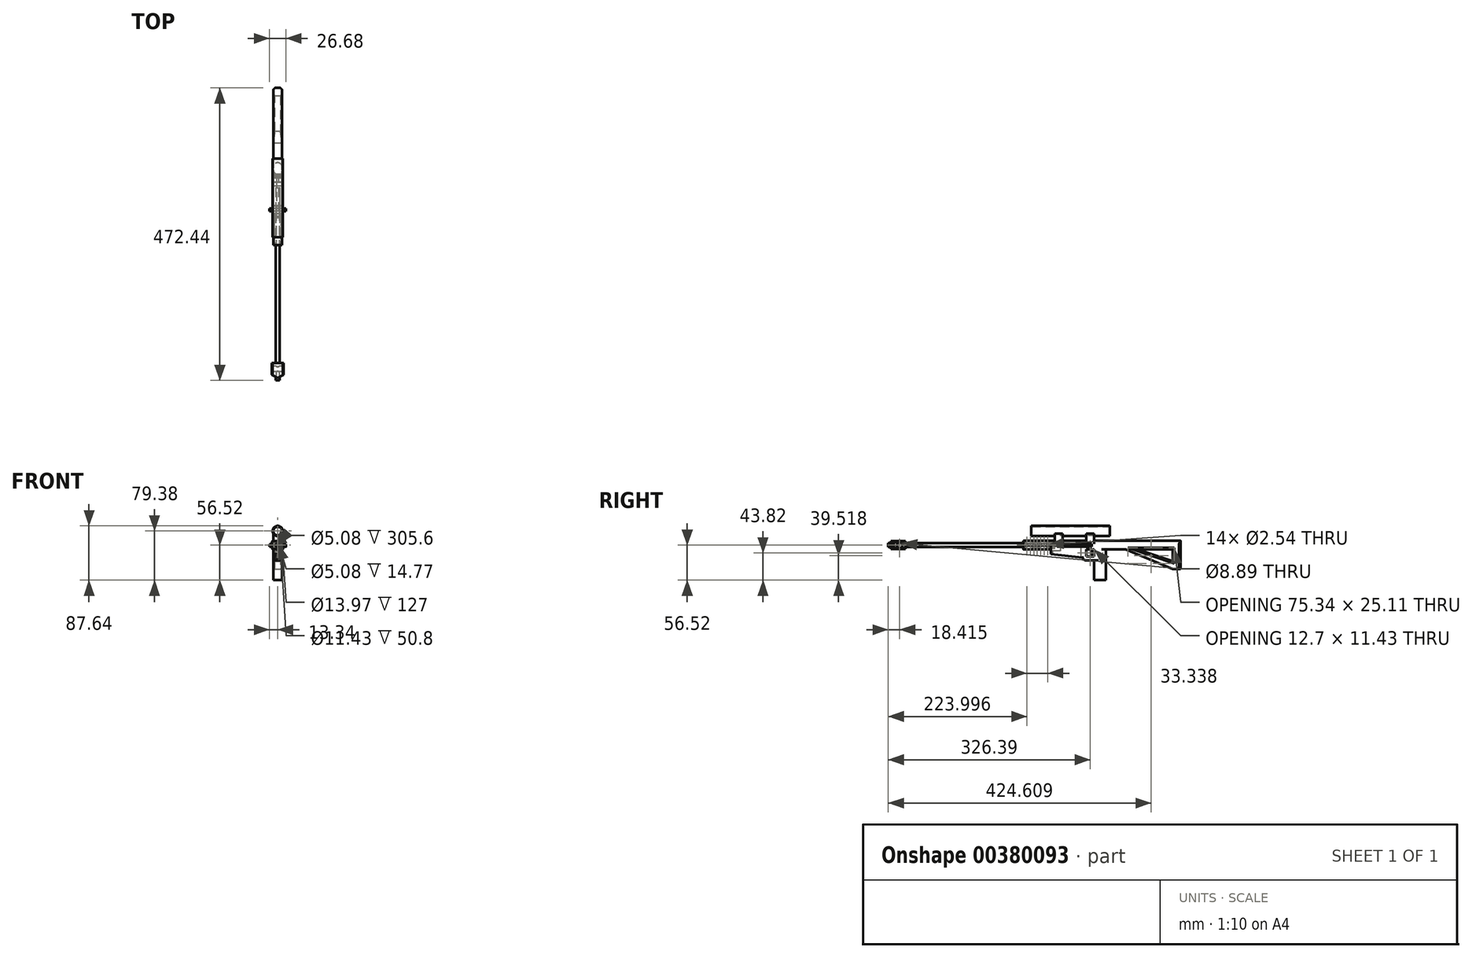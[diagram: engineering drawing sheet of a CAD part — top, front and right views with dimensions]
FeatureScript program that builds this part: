
annotation { "Feature Type Name" : "Feature", "Feature Type Description" : "" }
export const myFeature = defineFeature(function(context is Context, id is Id, definition is map)
    precondition{}
    {
        {
            var Q0;
            Q0=qCreatedBy(makeId("Front.planeOp"),FACE);
            var sketch = newSketch(context, id + "F0", { "sketchPlane" : qUnion([Q0])});
            skLineSegment(sketch, "E0.bottom", {"start": v(9.53, -6.35) * mm, "end": v(-9.53, -6.35) * mm});
            skLineSegment(sketch, "E0.top", {"start": v(9.53, 6.35) * mm, "end": v(-9.53, 6.35) * mm});
            skLineSegment(sketch, "E0.left", {"start": v(9.53, -6.35) * mm, "end": v(9.53, 6.35) * mm});
            skLineSegment(sketch, "E0.right", {"start": v(-9.53, -6.35) * mm, "end": v(-9.53, 6.35) * mm});
            skPoint(sketch, "E0.middle", {"position": v(0, 0) * mm});
            skSolve(sketch);
        }
        {
            var Q0;
            Q0 = qSketchRegion(id + "F0", true);
            extrude(context, id + "F1", {"entities" : qUnion([Q0]), "depth" : 25.4 * mm});
        }
        {
            var Q0;
            Q0=makeQuery(id+"F1.opExtrude","CAP_FACE",FACE,{"disambiguationData":[OSD([sQuery(id+"F0.wireOp",EDGE,"E0.bottom"),sQuery(id+"F0.wireOp",EDGE,"E0.top"),sQuery(id+"F0.wireOp",EDGE,"E0.left"),sQuery(id+"F0.wireOp",EDGE,"E0.right")])],"isStart":true});
            var sketch = newSketch(context, id + "F2", { "sketchPlane" : qUnion([Q0])});
            skCircle(sketch, "E1", {"center": v(0, 0) * mm, "radius": 3.18 * mm});
            skSolve(sketch);
        }
        {
            var Q0;
            Q0 = qSketchRegion(id + "F2", true);
            extrude(context, id + "F3", {"entities" : qUnion([Q0]), "operationType" : NewBodyOperationType.ADD, "depth" : 190.5 * mm});
        }
        {
            var Q0;
            Q0=makeQuery(id+"F3.opExtrude","CAP_FACE",FACE,{"disambiguationData":[OSD([sQuery(id+"F2.wireOp",EDGE,"E1")])],"isStart":false});
            var sketch = newSketch(context, id + "F4", { "sketchPlane" : qUnion([Q0])});
            skLineSegment(sketch, "E2.bottom", {"start": v(6.99, -6.99) * mm, "end": v(-6.99, -6.99) * mm});
            skLineSegment(sketch, "E2.top", {"start": v(6.98, 6.99) * mm, "end": v(-6.98, 6.99) * mm});
            skLineSegment(sketch, "E2.left", {"start": v(6.99, -6.99) * mm, "end": v(6.99, 6.98) * mm});
            skLineSegment(sketch, "E2.right", {"start": v(-6.99, -6.99) * mm, "end": v(-6.99, 6.98) * mm});
            skPoint(sketch, "E2.middle", {"position": v(0, 0) * mm});
            skSolve(sketch);
        }
        {
            var Q0;
            Q0 = qSketchRegion(id + "F4", true);
            extrude(context, id + "F5", {"entities" : qUnion([Q0]), "operationType" : NewBodyOperationType.ADD, "depth" : 254 * mm});
        }
        {
            var Q0;
            Q0=makeQuery(id+"F5.opExtrude","SWEPT_FACE",FACE,{"disambiguationData":[OSD([sQuery(id+"F4.wireOp",EDGE,"E2.right")])]});
            var sketch = newSketch(context, id + "F6", { "sketchPlane" : qUnion([Q0])});
            skLineSegment(sketch, "E3", {"start": v(444.5, -6.99) * mm, "end": v(444.5, -38.74) * mm});
            skLineSegment(sketch, "E4", {"start": v(444.5, -38.74) * mm, "end": v(431.8, -38.74) * mm});
            skLineSegment(sketch, "E5", {"start": v(431.8, -38.74) * mm, "end": v(431.8, -6.99) * mm});
            skSolve(sketch);
        }
        {
            var Q0;
            Q0 = qSketchRegion(id + "F6", true);
            var Q1;
            {var subQ0=sQuery(id+"F6.wireOp",EDGE,"E3");Q1=makeQuery(id+"F6.imprint","IMPRINT",FACE,{"disambiguationData":[TD([[makeQuery(id+"F6.imprint","IMPRINT",EDGE,{"derivedFrom":subQ0}),-1.0]])]});}
            extrude(context, id + "F7", {"entities" : qUnion([Q0, Q1]), "operationType" : NewBodyOperationType.ADD, "depth" : -13.97 * mm});
        }
        {
            var Q0;
            {var subQ0=sQuery(id+"F4.wireOp",EDGE,"E2.right");Q0=makeQuery(id+"F7.boolean.opBoolean","MERGE",FACE,{"derivedFrom":[makeQuery(id+"F5.opExtrude","SWEPT_FACE",FACE,{"disambiguationData":[OSD([subQ0])]}),makeQuery(id+"F7.opExtrude","CAP_FACE",FACE,{"disambiguationData":[OSD([sQuery(id+"F4.wireOp",EDGE,"E2.bottom"),subQ0,sQuery(id+"F6.wireOp",EDGE,"E3"),sQuery(id+"F6.wireOp",EDGE,"E4"),sQuery(id+"F6.wireOp",EDGE,"E5")])],"isStart":true})]});}
            var sketch = newSketch(context, id + "F8", { "sketchPlane" : qUnion([Q0])});
            skLineSegment(sketch, "E6", {"start": v(431.8, -38.74) * mm, "end": v(355.6, -6.98) * mm});
            skLineSegment(sketch, "E7", {"start": v(431.8, -38.74) * mm, "end": v(431.8, -26.04) * mm});
            skLineSegment(sketch, "E8", {"start": v(431.8, -26.03) * mm, "end": v(374.65, -6.98) * mm});
            skLineSegment(sketch, "E9", {"start": v(374.65, -6.99) * mm, "end": v(355.6, -6.99) * mm});
            skSolve(sketch);
        }
        {
            var Q0;
            Q0 = qSketchRegion(id + "F8", true);
            extrude(context, id + "F9", {"entities" : qUnion([Q0]), "operationType" : NewBodyOperationType.ADD, "depth" : -13.97 * mm});
        }
        {
            var Q0;
            Q0=makeQuery(id+"F9.boolean.opBoolean","MERGE",FACE,{"derivedFrom":[makeQuery(id+"F7.boolean.opBoolean","MERGE",FACE,{"derivedFrom":[makeQuery(id+"F5.opExtrude","SWEPT_FACE",FACE,{"disambiguationData":[OSD([sQuery(id+"F4.wireOp",EDGE,"E2.left")])]}),makeQuery(id+"F7.opExtrude","CAP_FACE",FACE,{"disambiguationData":[OSD([sQuery(id+"F4.wireOp",EDGE,"E2.bottom"),sQuery(id+"F4.wireOp",EDGE,"E2.right"),sQuery(id+"F6.wireOp",EDGE,"E3"),sQuery(id+"F6.wireOp",EDGE,"E4"),sQuery(id+"F6.wireOp",EDGE,"E5")])],"isStart":false})]}),makeQuery(id+"F9.opExtrude","CAP_FACE",FACE,{"disambiguationData":[OSD([sQuery(id+"F8.wireOp",EDGE,"E6"),sQuery(id+"F8.wireOp",EDGE,"E7"),sQuery(id+"F8.wireOp",EDGE,"E8"),sQuery(id+"F8.wireOp",EDGE,"E9")])],"isStart":false})]});
            var sketch = newSketch(context, id + "F10", { "sketchPlane" : qUnion([Q0])});
            skLineSegment(sketch, "E10", {"start": v(-444.5, 6.98) * mm, "end": v(-190.5, 6.98) * mm});
            skLineSegment(sketch, "E11", {"start": v(-190.5, 6.98) * mm, "end": v(-317.5, 6.98) * mm});
            skLineSegment(sketch, "E12", {"start": v(-317.5, 6.98) * mm, "end": v(-317.5, -43.82) * mm});
            skLineSegment(sketch, "E13", {"start": v(-317.5, -43.82) * mm, "end": v(-304.8, -43.82) * mm});
            skLineSegment(sketch, "E14", {"start": v(-304.8, -43.82) * mm, "end": v(-304.8, 6.98) * mm});
            skLineSegment(sketch, "E15", {"start": v(-304.8, -18.42) * mm, "end": v(-292.1, -18.42) * mm});
            skLineSegment(sketch, "E16", {"start": v(-292.1, -18.42) * mm, "end": v(-292.1, -6.99) * mm});
            skLineSegment(sketch, "E17", {"start": v(-292.1, -6.99) * mm, "end": v(-285.75, -6.99) * mm});
            skLineSegment(sketch, "E18", {"start": v(-285.75, -6.99) * mm, "end": v(-285.75, -24.77) * mm});
            skLineSegment(sketch, "E19", {"start": v(-285.75, -24.77) * mm, "end": v(-304.8, -24.77) * mm});
            skLineSegment(sketch, "E20", {"start": v(-285.75, -6.99) * mm, "end": v(-280.67, -6.99) * mm});
            skLineSegment(sketch, "E21", {"start": v(-304.8, -43.82) * mm, "end": v(-304.8, -56.52) * mm});
            skLineSegment(sketch, "E22", {"start": v(-317.5, -43.82) * mm, "end": v(-317.5, -56.52) * mm});
            skLineSegment(sketch, "E23", {"start": v(-304.8, -56.52) * mm, "end": v(-317.5, -56.52) * mm});
            skLineSegment(sketch, "E24", {"start": v(-317.5, -56.52) * mm, "end": v(-323.85, -56.52) * mm});
            skLineSegment(sketch, "E25", {"start": v(-323.85, -56.52) * mm, "end": v(-323.85, -6.99) * mm});
            skSolve(sketch);
        }
        {
            var Q0;
            Q0 = qSketchRegion(id + "F10", true);
            var Q1;
            {var subQ8=sQuery(id+"F10.wireOp",EDGE,"E22");Q1=makeQuery(id+"F10.imprint","IMPRINT",FACE,{"disambiguationData":[TD([[makeQuery(id+"F10.imprint","IMPRINT",EDGE,{"derivedFrom":subQ8}),-1.0]])]});}
            extrude(context, id + "F11", {"entities" : qUnion([Q0, Q1]), "operationType" : NewBodyOperationType.ADD, "depth" : -13.97 * mm});
        }
        {
            var Q0;
            Q0=makeQuery(id+"F11.opExtrude","SWEPT_EDGE",EDGE,{"disambiguationData":[OSD([sQuery(id+"F10.wireOp",EDGE,"E18"),sQuery(id+"F10.wireOp",EDGE,"E19")])]});
            fillet(context, id + "F12", {"entities" : qUnion([Q0]), "radius" : 6.35 * mm, "tangentPropagation" : true, "allowEdgeOverflow" : false});
        }
        {
            var Q0;
            Q0=makeQuery(id+"F11.boolean.opBoolean","MERGE",FACE,{"derivedFrom":[makeQuery(id+"F9.boolean.opBoolean","MERGE",FACE,{"derivedFrom":[makeQuery(id+"F7.boolean.opBoolean","MERGE",FACE,{"derivedFrom":[makeQuery(id+"F5.opExtrude","SWEPT_FACE",FACE,{"disambiguationData":[OSD([sQuery(id+"F4.wireOp",EDGE,"E2.left")])]}),makeQuery(id+"F7.opExtrude","CAP_FACE",FACE,{"disambiguationData":[OSD([sQuery(id+"F4.wireOp",EDGE,"E2.bottom"),sQuery(id+"F4.wireOp",EDGE,"E2.right"),sQuery(id+"F6.wireOp",EDGE,"E3"),sQuery(id+"F6.wireOp",EDGE,"E4"),sQuery(id+"F6.wireOp",EDGE,"E5")])],"isStart":false})]}),makeQuery(id+"F9.opExtrude","CAP_FACE",FACE,{"disambiguationData":[OSD([sQuery(id+"F8.wireOp",EDGE,"E6"),sQuery(id+"F8.wireOp",EDGE,"E7"),sQuery(id+"F8.wireOp",EDGE,"E8"),sQuery(id+"F8.wireOp",EDGE,"E9")])],"isStart":false})]}),makeQuery(id+"F11.opExtrude","CAP_FACE",FACE,{"disambiguationData":[OSD([sQuery(id+"F10.wireOp",EDGE,"E11"),sQuery(id+"F10.wireOp",EDGE,"E12"),sQuery(id+"F10.wireOp",EDGE,"E13"),sQuery(id+"F10.wireOp",EDGE,"E14"),sQuery(id+"F10.wireOp",EDGE,"E15"),sQuery(id+"F10.wireOp",EDGE,"E16"),sQuery(id+"F10.wireOp",EDGE,"E17"),sQuery(id+"F10.wireOp",EDGE,"E18"),sQuery(id+"F10.wireOp",EDGE,"E19")])],"isStart":true})]});
            var sketch = newSketch(context, id + "F13", { "sketchPlane" : qUnion([Q0])});
            skLineSegment(sketch, "E26", {"start": v(-234.95, -22.23) * mm, "end": v(-234.95, -6.99) * mm});
            skLineSegment(sketch, "E27", {"start": v(-234.95, -22.23) * mm, "end": v(-285.75, -22.23) * mm});
            skLineSegment(sketch, "E28", {"start": v(-285.75, -22.23) * mm, "end": v(-285.75, -6.99) * mm});
            skSolve(sketch);
        }
        {
            var Q0;
            Q0 = qSketchRegion(id + "F13", true);
            var Q1;
            {var subQ0=sQuery(id+"F13.wireOp",EDGE,"gqdgmxWL-FIIV-5ZZU-RBbH-KmW0Z6Do0HDY");Q1=makeQuery(id+"F13.imprint","IMPRINT",FACE,{"disambiguationData":[TD([[makeQuery(id+"F13.imprint","IMPRINT",EDGE,{"derivedFrom":subQ0}),1.0]])]});}
            var Q2;
            {var subQ17=sQuery(id+"F13.wireOp",EDGE,"E26");Q2=makeQuery(id+"F13.imprint","IMPRINT",FACE,{"disambiguationData":[TD([[makeQuery(id+"F13.imprint","IMPRINT",EDGE,{"derivedFrom":subQ17}),1.0]])]});}
            extrude(context, id + "F14", {"entities" : qUnion([Q0, Q1, Q2]), "operationType" : NewBodyOperationType.ADD, "depth" : -13.97 * mm});
        }
        {
            var Q0;
            {var subQ0=sQuery(id+"F4.wireOp",EDGE,"E2.left");var subQ1=sQuery(id+"F4.wireOp",EDGE,"E2.bottom");Q0=makeQuery(id+"F14.boolean.opBoolean","MERGE",FACE,{"derivedFrom":[makeQuery(id+"F11.boolean.opBoolean","MERGE",FACE,{"derivedFrom":[makeQuery(id+"F9.boolean.opBoolean","MERGE",FACE,{"derivedFrom":[makeQuery(id+"F7.boolean.opBoolean","MERGE",FACE,{"derivedFrom":[makeQuery(id+"F5.opExtrude","SWEPT_FACE",FACE,{"disambiguationData":[OSD([subQ0])]}),makeQuery(id+"F7.opExtrude","CAP_FACE",FACE,{"disambiguationData":[OSD([subQ1,sQuery(id+"F4.wireOp",EDGE,"E2.right"),sQuery(id+"F6.wireOp",EDGE,"E3"),sQuery(id+"F6.wireOp",EDGE,"E4"),sQuery(id+"F6.wireOp",EDGE,"E5")])],"isStart":false})]}),makeQuery(id+"F9.opExtrude","CAP_FACE",FACE,{"disambiguationData":[OSD([sQuery(id+"F8.wireOp",EDGE,"E6"),sQuery(id+"F8.wireOp",EDGE,"E7"),sQuery(id+"F8.wireOp",EDGE,"E8"),sQuery(id+"F8.wireOp",EDGE,"E9")])],"isStart":false})]}),makeQuery(id+"F11.opExtrude","CAP_FACE",FACE,{"disambiguationData":[OSD([sQuery(id+"F10.wireOp",EDGE,"E11"),sQuery(id+"F10.wireOp",EDGE,"E12"),sQuery(id+"F10.wireOp",EDGE,"E13"),sQuery(id+"F10.wireOp",EDGE,"E14"),sQuery(id+"F10.wireOp",EDGE,"E15"),sQuery(id+"F10.wireOp",EDGE,"E16"),sQuery(id+"F10.wireOp",EDGE,"E17"),sQuery(id+"F10.wireOp",EDGE,"E18"),sQuery(id+"F10.wireOp",EDGE,"E19")])],"isStart":true})]}),makeQuery(id+"F14.opExtrude","CAP_FACE",FACE,{"disambiguationData":[OSD([subQ1,subQ0,sQuery(id+"F13.wireOp",EDGE,"gqdgmxWL-FIIV-5ZZU-RBbH-KmW0Z6Do0HDY"),sQuery(id+"F13.wireOp",EDGE,"u0oC4iEc-4FHG-jWvm-i2Hm-SS8I0tg0rfsX"),sQuery(id+"F13.wireOp",EDGE,"E26")])],"isStart":true})]});}
            var sketch = newSketch(context, id + "F15", { "sketchPlane" : qUnion([Q0])});
            skLineSegment(sketch, "E29", {"start": v(-304.8, -6.99) * mm, "end": v(-304.8, 18.41) * mm});
            skLineSegment(sketch, "E30", {"start": v(-292.1, -6.99) * mm, "end": v(-292.1, 18.41) * mm});
            skLineSegment(sketch, "E31", {"start": v(-304.8, 18.41) * mm, "end": v(-292.1, 18.41) * mm});
            skLineSegment(sketch, "E32", {"start": v(-292.1, -6.99) * mm, "end": v(-254, -6.99) * mm});
            skLineSegment(sketch, "E33", {"start": v(-254, -6.99) * mm, "end": v(-254, 18.41) * mm});
            skLineSegment(sketch, "E34", {"start": v(-254, 18.41) * mm, "end": v(-241.3, 18.41) * mm});
            skLineSegment(sketch, "E35", {"start": v(-241.3, 18.41) * mm, "end": v(-241.3, 6.98) * mm});
            skSolve(sketch);
        }
        {
            var Q0;
            Q0 = qSketchRegion(id + "F15", true);
            var Q1;
            {var subQ0=sQuery(id+"F15.wireOp",EDGE,"E31");Q1=makeQuery(id+"F15.imprint","IMPRINT",FACE,{"disambiguationData":[TD([[makeQuery(id+"F15.imprint","IMPRINT",EDGE,{"derivedFrom":subQ0}),-1.0]])]});}
            var Q2;
            {var subQ0=sQuery(id+"F15.wireOp",EDGE,"E34");Q2=makeQuery(id+"F15.imprint","IMPRINT",FACE,{"disambiguationData":[TD([[makeQuery(id+"F15.imprint","IMPRINT",EDGE,{"derivedFrom":subQ0}),-1.0]])]});}
            extrude(context, id + "F16", {"entities" : qUnion([Q0, Q1, Q2]), "operationType" : NewBodyOperationType.ADD, "depth" : -13.97 * mm});
        }
        {
            var Q0;
            Q0=makeQuery(id+"F16.opExtrude","SWEPT_FACE",FACE,{"disambiguationData":[OSD([sQuery(id+"F15.wireOp",EDGE,"E29")])]});
            var sketch = newSketch(context, id + "F17", { "sketchPlane" : qUnion([Q0])});
            skLineSegment(sketch, "E36", {"start": v(0, 0) * mm, "end": v(0, 22.86) * mm});
            skPoint(sketch, "E36.endSnap0", {"position": v(0, 18.41) * mm});
            skCircle(sketch, "E37", {"center": v(0, 22.86) * mm, "radius": 8.26 * mm});
            skSolve(sketch);
        }
        {
            var Q0;
            Q0 = qSketchRegion(id + "F17", true);
            extrude(context, id + "F18", {"entities" : qUnion([Q0]), "operationType" : NewBodyOperationType.ADD, "depth" : 25.4 * mm, "hasSecondDirection" : true, "secondDirectionOppositeDirection" : true, "secondDirectionDepth" : 101.6 * mm});
        }
        {
            var Q0;
            Q0=makeQuery(id+"F14.opExtrude","SWEPT_FACE",FACE,{"disambiguationData":[OSD([sQuery(id+"F13.wireOp",EDGE,"E27")])]});
            var sketch = newSketch(context, id + "F19", { "sketchPlane" : qUnion([Q0])});
            skLineSegment(sketch, "E38", {"start": v(-3.5, -283.21) * mm, "end": v(3.5, -283.21) * mm});
            skLineSegment(sketch, "E39", {"start": v(-3.5, -237.49) * mm, "end": v(3.5, -237.49) * mm});
            skLineSegment(sketch, "E40", {"start": v(-3.5, -283.21) * mm, "end": v(-3.5, -237.49) * mm});
            skLineSegment(sketch, "E41", {"start": v(3.5, -237.49) * mm, "end": v(3.5, -283.21) * mm});
            skLineSegment(sketch, "E42", {"start": v(3.5, -283.21) * mm, "end": v(3.5, -237.49) * mm});
            skLineSegment(sketch, "E43", {"start": v(3.5, -237.49) * mm, "end": v(-3.5, -237.49) * mm});
            skLineSegment(sketch, "E44", {"start": v(-3.5, -237.49) * mm, "end": v(-3.5, -283.21) * mm});
            skSolve(sketch);
        }
        {
            var Q0;
            Q0 = qSketchRegion(id + "F19", true);
            extrude(context, id + "F20", {"entities" : qUnion([Q0]), "operationType" : NewBodyOperationType.REMOVE, "oppositeDirection" : true, "depth" : 12.7 * mm});
        }
        {
            var Q0;
            Q0=makeQuery(id+"F14.opExtrude","SWEPT_EDGE",EDGE,{"disambiguationData":[OSD([sQuery(id+"F13.wireOp",EDGE,"E26"),sQuery(id+"F13.wireOp",EDGE,"E27")])]});
            chamfer(context, id + "F21", {"entities" : qUnion([Q0]), "chamferType" : ChamferType.OFFSET_ANGLE, "width" : 7.62 * mm, "oppositeDirection" : true, "angle" : 84 * degree, "tangentPropagation" : true});
        }
        {
            var Q0;
            Q0=makeQuery(id+"F7.boolean.opBoolean","MERGE",EDGE,{"derivedFrom":[makeQuery(id+"F5.opExtrude","CAP_EDGE",EDGE,{"disambiguationData":[OSD([sQuery(id+"F4.wireOp",EDGE,"E2.left")])],"isStart":false}),makeQuery(id+"F7.opExtrude","CAP_EDGE",EDGE,{"disambiguationData":[OSD([sQuery(id+"F6.wireOp",EDGE,"E3")])],"isStart":false})]});
            var Q1;
            Q1=makeQuery(id+"F7.boolean.opBoolean","MERGE",EDGE,{"derivedFrom":[makeQuery(id+"F5.opExtrude","CAP_EDGE",EDGE,{"disambiguationData":[OSD([sQuery(id+"F4.wireOp",EDGE,"E2.right")])],"isStart":false}),makeQuery(id+"F7.opExtrude","CAP_EDGE",EDGE,{"disambiguationData":[OSD([sQuery(id+"F6.wireOp",EDGE,"E3")])],"isStart":true})]});
            chamfer(context, id + "F22", {"entities" : qUnion([Q0, Q1]), "width" : 2.54 * mm, "tangentPropagation" : true});
        }
        {
            var Q0;
            {var subQ1=sQuery(id+"F4.wireOp",EDGE,"E2.left");var subQ2=sQuery(id+"F4.wireOp",EDGE,"E2.top");var subQ3=sQuery(id+"F6.wireOp",EDGE,"E3");Q0=makeQuery(id+"F16.boolean.opBoolean","SPLIT",EDGE,{"disambiguationData":[TD([makeQuery(id+"F7.opExtrude","SWEPT_FACE",FACE,{"disambiguationData":[OSD([subQ3])]})])],"derivedFrom":makeQuery(id+"F5.opExtrude","SWEPT_EDGE",EDGE,{"disambiguationData":[OSD([subQ2,subQ1])]})});}
            var Q1;
            {var subQ2=sQuery(id+"F4.wireOp",EDGE,"E2.top");var subQ3=sQuery(id+"F4.wireOp",EDGE,"E2.right");var subQ5=sQuery(id+"F6.wireOp",EDGE,"E3");Q1=makeQuery(id+"F16.boolean.opBoolean","SPLIT",EDGE,{"disambiguationData":[TD([makeQuery(id+"F7.opExtrude","SWEPT_FACE",FACE,{"disambiguationData":[OSD([subQ5])]})])],"derivedFrom":makeQuery(id+"F5.opExtrude","SWEPT_EDGE",EDGE,{"disambiguationData":[OSD([subQ2,subQ3])]})});}
            var Q2;
            {var subQ2=sQuery(id+"F4.wireOp",EDGE,"E2.left");var subQ3=sQuery(id+"F4.wireOp",EDGE,"E2.top");var subQ4=sQuery(id+"F15.wireOp",EDGE,"E30");Q2=makeQuery(id+"F16.boolean.opBoolean","SPLIT",EDGE,{"disambiguationData":[TD([makeQuery(id+"F16.opExtrude","SWEPT_FACE",FACE,{"disambiguationData":[OSD([subQ4])]})])],"derivedFrom":makeQuery(id+"F5.opExtrude","SWEPT_EDGE",EDGE,{"disambiguationData":[OSD([subQ3,subQ2])]})});}
            var Q3;
            {var subQ0=sQuery(id+"F4.wireOp",EDGE,"E2.right");var subQ2=sQuery(id+"F4.wireOp",EDGE,"E2.top");var subQ5=sQuery(id+"F15.wireOp",EDGE,"E30");Q3=makeQuery(id+"F16.boolean.opBoolean","SPLIT",EDGE,{"disambiguationData":[TD([makeQuery(id+"F16.opExtrude","SWEPT_FACE",FACE,{"disambiguationData":[OSD([subQ5])]})])],"derivedFrom":makeQuery(id+"F5.opExtrude","SWEPT_EDGE",EDGE,{"disambiguationData":[OSD([subQ2,subQ0])]})});}
            fillet(context, id + "F23", {"entities" : qUnion([Q0, Q1, Q2, Q3]), "radius" : 5.08 * mm, "tangentPropagation" : true, "allowEdgeOverflow" : false});
        }
        {
            var Q0;
            Q0=makeQuery(id+"F1.opExtrude","CAP_EDGE",EDGE,{"disambiguationData":[OSD([sQuery(id+"F0.wireOp",EDGE,"E0.left")])],"isStart":false});
            var Q1;
            Q1=makeQuery(id+"F1.opExtrude","CAP_EDGE",EDGE,{"disambiguationData":[OSD([sQuery(id+"F0.wireOp",EDGE,"E0.right")])],"isStart":false});
            chamfer(context, id + "F24", {"entities" : qUnion([Q0, Q1]), "chamferType" : ChamferType.OFFSET_ANGLE, "width" : 6.35 * mm, "oppositeDirection" : true, "angle" : 64 * degree, "tangentPropagation" : true});
        }
        {
            var Q0;
            Q0=qCreatedBy(makeId("Front.planeOp"),FACE);
            var sketch = newSketch(context, id + "F25", { "sketchPlane" : qUnion([Q0])});
            skCircle(sketch, "E45", {"center": v(0, 0) * mm, "radius": 3.18 * mm});
            skSolve(sketch);
        }
        {
            var Q0;
            Q0 = qSketchRegion(id + "F25", true);
            extrude(context, id + "F26", {"entities" : qUnion([Q0]), "operationType" : NewBodyOperationType.ADD, "depth" : 27.94 * mm});
        }
        {
            var Q0;
            Q0=makeQuery(id+"F1.opExtrude","SWEPT_FACE",FACE,{"disambiguationData":[OSD([sQuery(id+"F0.wireOp",EDGE,"E0.right")])]});
            var sketch = newSketch(context, id + "F27", { "sketchPlane" : qUnion([Q0])});
            skLineSegment(sketch, "E46", {"start": v(0, 0) * mm, "end": v(19.05, 0) * mm});
            skLineSegment(sketch, "E47", {"start": v(19.05, 0) * mm, "end": v(9.53, 0) * mm});
            skCircle(sketch, "E48", {"center": v(9.53, 0) * mm, "radius": 4.45 * mm});
            skSolve(sketch);
        }
        {
            var Q0;
            Q0 = qSketchRegion(id + "F27", true);
            extrude(context, id + "F28", {"entities" : qUnion([Q0]), "operationType" : NewBodyOperationType.REMOVE, "oppositeDirection" : true, "depth" : 50.8 * mm});
        }
        {
            var Q0;
            Q0=makeQuery(id+"F26.opExtrude","CAP_FACE",FACE,{"disambiguationData":[OSD([sQuery(id+"F25.wireOp",EDGE,"E45")])],"isStart":false});
            var sketch = newSketch(context, id + "F29", { "sketchPlane" : qUnion([Q0])});
            skCircle(sketch, "E49", {"center": v(0, 0) * mm, "radius": 2.54 * mm});
            skSolve(sketch);
        }
        {
            var Q0;
            Q0 = qSketchRegion(id + "F29", true);
            extrude(context, id + "F30", {"entities" : qUnion([Q0]), "operationType" : NewBodyOperationType.REMOVE, "oppositeDirection" : true, "depth" : 327.66 * mm});
        }
        {
            var Q0;
            {var subQ0=sQuery(id+"F4.wireOp",EDGE,"E2.left");var subQ1=sQuery(id+"F4.wireOp",EDGE,"E2.top");var subQ2=sQuery(id+"F4.wireOp",EDGE,"E2.bottom");Q0=makeQuery(id+"F16.boolean.opBoolean","MERGE",FACE,{"derivedFrom":[makeQuery(id+"F14.boolean.opBoolean","MERGE",FACE,{"derivedFrom":[makeQuery(id+"F11.boolean.opBoolean","MERGE",FACE,{"derivedFrom":[makeQuery(id+"F9.boolean.opBoolean","MERGE",FACE,{"derivedFrom":[makeQuery(id+"F7.boolean.opBoolean","MERGE",FACE,{"derivedFrom":[makeQuery(id+"F5.opExtrude","SWEPT_FACE",FACE,{"disambiguationData":[OSD([subQ0])]}),makeQuery(id+"F7.opExtrude","CAP_FACE",FACE,{"disambiguationData":[OSD([subQ2,sQuery(id+"F4.wireOp",EDGE,"E2.right"),sQuery(id+"F6.wireOp",EDGE,"E3"),sQuery(id+"F6.wireOp",EDGE,"E4"),sQuery(id+"F6.wireOp",EDGE,"E5")])],"isStart":false})]}),makeQuery(id+"F9.opExtrude","CAP_FACE",FACE,{"disambiguationData":[OSD([sQuery(id+"F8.wireOp",EDGE,"E6"),sQuery(id+"F8.wireOp",EDGE,"E7"),sQuery(id+"F8.wireOp",EDGE,"E8"),sQuery(id+"F8.wireOp",EDGE,"E9")])],"isStart":false})]}),makeQuery(id+"F11.opExtrude","CAP_FACE",FACE,{"disambiguationData":[OSD([sQuery(id+"F10.wireOp",EDGE,"E11"),sQuery(id+"F10.wireOp",EDGE,"E12"),sQuery(id+"F10.wireOp",EDGE,"E13"),sQuery(id+"F10.wireOp",EDGE,"E14"),sQuery(id+"F10.wireOp",EDGE,"E15"),sQuery(id+"F10.wireOp",EDGE,"E16"),sQuery(id+"F10.wireOp",EDGE,"E17"),sQuery(id+"F10.wireOp",EDGE,"E18"),sQuery(id+"F10.wireOp",EDGE,"E19")])],"isStart":true})]}),makeQuery(id+"F14.opExtrude","CAP_FACE",FACE,{"disambiguationData":[OSD([subQ2,subQ0,sQuery(id+"F13.wireOp",EDGE,"E26"),sQuery(id+"F13.wireOp",EDGE,"E27"),sQuery(id+"F13.wireOp",EDGE,"E28")])],"isStart":true})]}),makeQuery(id+"F16.opExtrude","CAP_FACE",FACE,{"disambiguationData":[OSD([subQ1,subQ0,sQuery(id+"F15.wireOp",EDGE,"E29"),sQuery(id+"F15.wireOp",EDGE,"E30"),sQuery(id+"F15.wireOp",EDGE,"E31")])],"isStart":true}),makeQuery(id+"F16.opExtrude","CAP_FACE",FACE,{"disambiguationData":[OSD([subQ1,subQ0,sQuery(id+"F15.wireOp",EDGE,"E33"),sQuery(id+"F15.wireOp",EDGE,"E34"),sQuery(id+"F15.wireOp",EDGE,"E35")])],"isStart":true})]});}
            var sketch = newSketch(context, id + "F31", { "sketchPlane" : qUnion([Q0])});
            skLineSegment(sketch, "E50", {"start": v(-300.99, 1.9) * mm, "end": v(-300.99, -2.54) * mm});
            skLineSegment(sketch, "E51", {"start": v(-300.99, -2.54) * mm, "end": v(-245.1, -2.54) * mm});
            skLineSegment(sketch, "E52", {"start": v(-300.99, 1.9) * mm, "end": v(-245.1, 1.9) * mm});
            skLineSegment(sketch, "E53", {"start": v(-245.1, 1.9) * mm, "end": v(-245.1, -2.54) * mm});
            skSolve(sketch);
        }
        {
            var Q0;
            Q0 = qSketchRegion(id + "F31", true);
            extrude(context, id + "F32", {"entities" : qUnion([Q0]), "operationType" : NewBodyOperationType.REMOVE, "oppositeDirection" : true, "depth" : 25.4 * mm});
        }
        {
            var Q0;
            {var subQ0=sQuery(id+"F4.wireOp",EDGE,"E2.left");var subQ1=sQuery(id+"F4.wireOp",EDGE,"E2.top");var subQ2=sQuery(id+"F4.wireOp",EDGE,"E2.bottom");Q0=makeQuery(id+"F16.boolean.opBoolean","MERGE",FACE,{"derivedFrom":[makeQuery(id+"F14.boolean.opBoolean","MERGE",FACE,{"derivedFrom":[makeQuery(id+"F11.boolean.opBoolean","MERGE",FACE,{"derivedFrom":[makeQuery(id+"F9.boolean.opBoolean","MERGE",FACE,{"derivedFrom":[makeQuery(id+"F7.boolean.opBoolean","MERGE",FACE,{"derivedFrom":[makeQuery(id+"F5.opExtrude","SWEPT_FACE",FACE,{"disambiguationData":[OSD([subQ0])]}),makeQuery(id+"F7.opExtrude","CAP_FACE",FACE,{"disambiguationData":[OSD([subQ2,sQuery(id+"F4.wireOp",EDGE,"E2.right"),sQuery(id+"F6.wireOp",EDGE,"E3"),sQuery(id+"F6.wireOp",EDGE,"E4"),sQuery(id+"F6.wireOp",EDGE,"E5")])],"isStart":false})]}),makeQuery(id+"F9.opExtrude","CAP_FACE",FACE,{"disambiguationData":[OSD([sQuery(id+"F8.wireOp",EDGE,"E6"),sQuery(id+"F8.wireOp",EDGE,"E7"),sQuery(id+"F8.wireOp",EDGE,"E8"),sQuery(id+"F8.wireOp",EDGE,"E9")])],"isStart":false})]}),makeQuery(id+"F11.opExtrude","CAP_FACE",FACE,{"disambiguationData":[OSD([sQuery(id+"F10.wireOp",EDGE,"E11"),sQuery(id+"F10.wireOp",EDGE,"E12"),sQuery(id+"F10.wireOp",EDGE,"E13"),sQuery(id+"F10.wireOp",EDGE,"E14"),sQuery(id+"F10.wireOp",EDGE,"E15"),sQuery(id+"F10.wireOp",EDGE,"E16"),sQuery(id+"F10.wireOp",EDGE,"E17"),sQuery(id+"F10.wireOp",EDGE,"E18"),sQuery(id+"F10.wireOp",EDGE,"E19")])],"isStart":true})]}),makeQuery(id+"F14.opExtrude","CAP_FACE",FACE,{"disambiguationData":[OSD([subQ2,subQ0,sQuery(id+"F13.wireOp",EDGE,"E26"),sQuery(id+"F13.wireOp",EDGE,"E27"),sQuery(id+"F13.wireOp",EDGE,"E28")])],"isStart":true})]}),makeQuery(id+"F16.opExtrude","CAP_FACE",FACE,{"disambiguationData":[OSD([subQ1,subQ0,sQuery(id+"F15.wireOp",EDGE,"E29"),sQuery(id+"F15.wireOp",EDGE,"E30"),sQuery(id+"F15.wireOp",EDGE,"E31")])],"isStart":true}),makeQuery(id+"F16.opExtrude","CAP_FACE",FACE,{"disambiguationData":[OSD([subQ1,subQ0,sQuery(id+"F15.wireOp",EDGE,"E33"),sQuery(id+"F15.wireOp",EDGE,"E34"),sQuery(id+"F15.wireOp",EDGE,"E35")])],"isStart":true})]});}
            var sketch = newSketch(context, id + "F33", { "sketchPlane" : qUnion([Q0])});
            skLineSegment(sketch, "E54", {"start": v(-245.1, -0.32) * mm, "end": v(-247.4, -0.32) * mm});
            skCircle(sketch, "E55", {"center": v(-247.4, -0.32) * mm, "radius": 2.16 * mm});
            skLineSegment(sketch, "E56", {"start": v(-247.4, -1.33) * mm, "end": v(-247.4, -0.32) * mm});
            skLineSegment(sketch, "E57", {"start": v(-247.4, -0.32) * mm, "end": v(-247.4, 0.7) * mm});
            skLineSegment(sketch, "E58", {"start": v(-247.4, 0.7) * mm, "end": v(-245.1, 0.7) * mm});
            skLineSegment(sketch, "E59", {"start": v(-247.4, -1.33) * mm, "end": v(-245.1, -1.33) * mm});
            skLineSegment(sketch, "E60", {"start": v(-245.1, -1.33) * mm, "end": v(-245.1, -0.32) * mm});
            skLineSegment(sketch, "E61", {"start": v(-245.1, 0.7) * mm, "end": v(-245.1, -0.32) * mm});
            skSolve(sketch);
        }
        {
            var Q0;
            Q0 = qSketchRegion(id + "F33", true);
            extrude(context, id + "F34", {"entities" : qUnion([Q0]), "operationType" : NewBodyOperationType.ADD, "depth" : -13.97 * mm});
        }
        {
            var Q0;
            {var subQ0=sQuery(id+"F4.wireOp",EDGE,"E2.left");var subQ1=sQuery(id+"F4.wireOp",EDGE,"E2.top");var subQ2=sQuery(id+"F4.wireOp",EDGE,"E2.bottom");var subQ3=sQuery(id+"F4.wireOp",EDGE,"E2.right");Q0=makeQuery(id+"F34.boolean.opBoolean","MERGE",FACE,{"derivedFrom":[makeQuery(id+"F16.boolean.opBoolean","MERGE",FACE,{"derivedFrom":[makeQuery(id+"F14.boolean.opBoolean","MERGE",FACE,{"derivedFrom":[makeQuery(id+"F11.boolean.opBoolean","MERGE",FACE,{"derivedFrom":[makeQuery(id+"F9.boolean.opBoolean","MERGE",FACE,{"derivedFrom":[makeQuery(id+"F7.boolean.opBoolean","MERGE",FACE,{"derivedFrom":[makeQuery(id+"F5.opExtrude","SWEPT_FACE",FACE,{"disambiguationData":[OSD([subQ3])]}),makeQuery(id+"F7.opExtrude","CAP_FACE",FACE,{"disambiguationData":[OSD([subQ2,subQ3,sQuery(id+"F6.wireOp",EDGE,"E3"),sQuery(id+"F6.wireOp",EDGE,"E4"),sQuery(id+"F6.wireOp",EDGE,"E5")])],"isStart":true})]}),makeQuery(id+"F9.opExtrude","CAP_FACE",FACE,{"disambiguationData":[OSD([sQuery(id+"F8.wireOp",EDGE,"E6"),sQuery(id+"F8.wireOp",EDGE,"E7"),sQuery(id+"F8.wireOp",EDGE,"E8"),sQuery(id+"F8.wireOp",EDGE,"E9")])],"isStart":true})]}),makeQuery(id+"F11.opExtrude","CAP_FACE",FACE,{"disambiguationData":[OSD([sQuery(id+"F10.wireOp",EDGE,"E11"),sQuery(id+"F10.wireOp",EDGE,"E12"),sQuery(id+"F10.wireOp",EDGE,"E13"),sQuery(id+"F10.wireOp",EDGE,"E14"),sQuery(id+"F10.wireOp",EDGE,"E15"),sQuery(id+"F10.wireOp",EDGE,"E16"),sQuery(id+"F10.wireOp",EDGE,"E17"),sQuery(id+"F10.wireOp",EDGE,"E18"),sQuery(id+"F10.wireOp",EDGE,"E19")])],"isStart":false})]}),makeQuery(id+"F14.opExtrude","CAP_FACE",FACE,{"disambiguationData":[OSD([subQ2,subQ0,sQuery(id+"F13.wireOp",EDGE,"E26"),sQuery(id+"F13.wireOp",EDGE,"E27"),sQuery(id+"F13.wireOp",EDGE,"E28")])],"isStart":false})]}),makeQuery(id+"F16.opExtrude","CAP_FACE",FACE,{"disambiguationData":[OSD([subQ1,subQ0,sQuery(id+"F15.wireOp",EDGE,"E29"),sQuery(id+"F15.wireOp",EDGE,"E30"),sQuery(id+"F15.wireOp",EDGE,"E31")])],"isStart":false}),makeQuery(id+"F16.opExtrude","CAP_FACE",FACE,{"disambiguationData":[OSD([subQ1,subQ0,sQuery(id+"F15.wireOp",EDGE,"E33"),sQuery(id+"F15.wireOp",EDGE,"E34"),sQuery(id+"F15.wireOp",EDGE,"E35")])],"isStart":false})]}),makeQuery(id+"F34.opExtrude","CAP_FACE",FACE,{"disambiguationData":[OSD([sQuery(id+"F33.wireOp",EDGE,"E55"),sQuery(id+"F33.wireOp",EDGE,"E58"),sQuery(id+"F33.wireOp",EDGE,"E59"),sQuery(id+"F33.wireOp",EDGE,"E60"),sQuery(id+"F33.wireOp",EDGE,"E61")])],"isStart":false})]});}
            var sketch = newSketch(context, id + "F35", { "sketchPlane" : qUnion([Q0])});
            skCircle(sketch, "E62", {"center": v(247.4, -0.32) * mm, "radius": 2.16 * mm});
            skSolve(sketch);
        }
        {
            var Q0;
            Q0 = qSketchRegion(id + "F35", true);
            extrude(context, id + "F36", {"entities" : qUnion([Q0]), "operationType" : NewBodyOperationType.ADD, "depth" : 6.35 * mm});
        }
        {
            var Q0;
            Q0=makeQuery(id+"F11.opExtrude","CAP_EDGE",EDGE,{"disambiguationData":[OSD([sQuery(id+"F10.wireOp",EDGE,"E25")])],"isStart":true});
            var Q1;
            Q1=makeQuery(id+"F11.opExtrude","CAP_EDGE",EDGE,{"disambiguationData":[OSD([sQuery(id+"F10.wireOp",EDGE,"E14"),sQuery(id+"F10.wireOp",EDGE,"E21")])],"isStart":true});
            var Q2;
            Q2=makeQuery(id+"F11.opExtrude","CAP_EDGE",EDGE,{"disambiguationData":[OSD([sQuery(id+"F10.wireOp",EDGE,"E14"),sQuery(id+"F10.wireOp",EDGE,"E21")])],"isStart":false});
            var Q3;
            Q3=makeQuery(id+"F11.opExtrude","CAP_EDGE",EDGE,{"disambiguationData":[OSD([sQuery(id+"F10.wireOp",EDGE,"E25")])],"isStart":false});
            fillet(context, id + "F37", {"entities" : qUnion([Q0, Q1, Q2, Q3]), "radius" : 7 * mm, "tangentPropagation" : true, "allowEdgeOverflow" : false});
        }
        {
            var Q0;
            {var subQ0=sQuery(id+"F4.wireOp",EDGE,"E2.left");var subQ1=sQuery(id+"F4.wireOp",EDGE,"E2.top");var subQ2=sQuery(id+"F4.wireOp",EDGE,"E2.bottom");Q0=makeQuery(id+"F34.boolean.opBoolean","MERGE",FACE,{"derivedFrom":[makeQuery(id+"F16.boolean.opBoolean","MERGE",FACE,{"derivedFrom":[makeQuery(id+"F14.boolean.opBoolean","MERGE",FACE,{"derivedFrom":[makeQuery(id+"F11.boolean.opBoolean","MERGE",FACE,{"derivedFrom":[makeQuery(id+"F9.boolean.opBoolean","MERGE",FACE,{"derivedFrom":[makeQuery(id+"F7.boolean.opBoolean","MERGE",FACE,{"derivedFrom":[makeQuery(id+"F5.opExtrude","SWEPT_FACE",FACE,{"disambiguationData":[OSD([subQ0])]}),makeQuery(id+"F7.opExtrude","CAP_FACE",FACE,{"disambiguationData":[OSD([subQ2,sQuery(id+"F4.wireOp",EDGE,"E2.right"),sQuery(id+"F6.wireOp",EDGE,"E3"),sQuery(id+"F6.wireOp",EDGE,"E4"),sQuery(id+"F6.wireOp",EDGE,"E5")])],"isStart":false})]}),makeQuery(id+"F9.opExtrude","CAP_FACE",FACE,{"disambiguationData":[OSD([sQuery(id+"F8.wireOp",EDGE,"E6"),sQuery(id+"F8.wireOp",EDGE,"E7"),sQuery(id+"F8.wireOp",EDGE,"E8"),sQuery(id+"F8.wireOp",EDGE,"E9")])],"isStart":false})]}),makeQuery(id+"F11.opExtrude","CAP_FACE",FACE,{"disambiguationData":[OSD([sQuery(id+"F10.wireOp",EDGE,"E11"),sQuery(id+"F10.wireOp",EDGE,"E12"),sQuery(id+"F10.wireOp",EDGE,"E13"),sQuery(id+"F10.wireOp",EDGE,"E14"),sQuery(id+"F10.wireOp",EDGE,"E15"),sQuery(id+"F10.wireOp",EDGE,"E16"),sQuery(id+"F10.wireOp",EDGE,"E17"),sQuery(id+"F10.wireOp",EDGE,"E18"),sQuery(id+"F10.wireOp",EDGE,"E19")])],"isStart":true})]}),makeQuery(id+"F14.opExtrude","CAP_FACE",FACE,{"disambiguationData":[OSD([subQ2,subQ0,sQuery(id+"F13.wireOp",EDGE,"E26"),sQuery(id+"F13.wireOp",EDGE,"E27"),sQuery(id+"F13.wireOp",EDGE,"E28")])],"isStart":true})]}),makeQuery(id+"F16.opExtrude","CAP_FACE",FACE,{"disambiguationData":[OSD([subQ1,subQ0,sQuery(id+"F15.wireOp",EDGE,"E29"),sQuery(id+"F15.wireOp",EDGE,"E30"),sQuery(id+"F15.wireOp",EDGE,"E31")])],"isStart":true}),makeQuery(id+"F16.opExtrude","CAP_FACE",FACE,{"disambiguationData":[OSD([subQ1,subQ0,sQuery(id+"F15.wireOp",EDGE,"E33"),sQuery(id+"F15.wireOp",EDGE,"E34"),sQuery(id+"F15.wireOp",EDGE,"E35")])],"isStart":true})]}),makeQuery(id+"F34.opExtrude","CAP_FACE",FACE,{"disambiguationData":[OSD([sQuery(id+"F33.wireOp",EDGE,"E55"),sQuery(id+"F33.wireOp",EDGE,"E58"),sQuery(id+"F33.wireOp",EDGE,"E59"),sQuery(id+"F33.wireOp",EDGE,"E60"),sQuery(id+"F33.wireOp",EDGE,"E61")])],"isStart":true})]});}
            var sketch = newSketch(context, id + "F38", { "sketchPlane" : qUnion([Q0])});
            skLineSegment(sketch, "E63", {"start": v(-303.21, -6.99) * mm, "end": v(-292.1, -6.99) * mm});
            skLineSegment(sketch, "E64", {"start": v(-292.1, -6.99) * mm, "end": v(-298.45, -6.99) * mm});
            skLineSegment(sketch, "E65", {"start": v(-298.45, -6.99) * mm, "end": v(-295.28, -6.99) * mm});
            skLineSegment(sketch, "E66", {"start": v(-295.28, -6.99) * mm, "end": v(-298.45, -6.99) * mm});
            skLineSegment(sketch, "E67", {"start": v(-298.45, -6.99) * mm, "end": v(-303.21, -6.99) * mm});
            skLineSegment(sketch, "E68", {"start": v(-303.21, -6.98) * mm, "end": v(-300.83, -6.98) * mm});
            skLineSegment(sketch, "E69", {"start": v(-300.83, -6.99) * mm, "end": v(-302.02, -6.99) * mm});
            skArc(sketch, "E70", {"start": v(-302.02, -6.99) * mm, "mid": v(-301.92, -12.37) * mm, "end": v(-298.94, -16.86) * mm});
            skArc(sketch, "E71", {"start": v(-300.83, -6.99) * mm, "mid": v(-300.52, -12.04) * mm, "end": v(-298.94, -16.86) * mm});
            skLineSegment(sketch, "E72", {"start": v(-302.02, -6.98) * mm, "end": v(-300.83, -6.98) * mm});
            skSolve(sketch);
        }
        {
            var Q0;
            Q0 = qSketchRegion(id + "F38", true);
            extrude(context, id + "F39", {"entities" : qUnion([Q0]), "operationType" : NewBodyOperationType.ADD, "depth" : -13.97 * mm, "hasSecondDirection" : true, "secondDirectionOppositeDirection" : true, "secondDirectionDepth" : 12.7 * mm});
        }
        {
            var Q0;
            Q0=makeQuery(id+"F39.opExtrude","CAP_FACE",FACE,{"disambiguationData":[OSD([sQuery(id+"F38.wireOp",EDGE,"E70"),sQuery(id+"F38.wireOp",EDGE,"E71"),sQuery(id+"F38.wireOp",EDGE,"E72")])],"isStart":true});
            extrude(context, id + "F40", {"entities" : qUnion([Q0]), "operationType" : NewBodyOperationType.ADD, "depth" : 12.7 * mm});
        }
        {
            var Q0;
            Q0=makeQuery(id+"F18.opExtrude","CAP_FACE",FACE,{"disambiguationData":[OSD([sQuery(id+"F17.wireOp",EDGE,"E37")])],"isStart":false});
            var sketch = newSketch(context, id + "F41", { "sketchPlane" : qUnion([Q0])});
            skCircle(sketch, "E73", {"center": v(0, 22.86) * mm, "radius": 6.99 * mm});
            skSolve(sketch);
        }
        {
            var Q0;
            Q0 = qSketchRegion(id + "F41", true);
            extrude(context, id + "F42", {"entities" : qUnion([Q0]), "operationType" : NewBodyOperationType.REMOVE, "oppositeDirection" : true, "depth" : 177.8 * mm});
        }
        {
            var Q0;
            {var subQ0=sQuery(id+"F4.wireOp",EDGE,"E2.right");var subQ1=sQuery(id+"F4.wireOp",EDGE,"E2.bottom");var subQ4=sQuery(id+"F10.wireOp",EDGE,"E18");var subQ7=sQuery(id+"F8.wireOp",EDGE,"E6");Q0=makeQuery(id+"F11.boolean.opBoolean","SPLIT",EDGE,{"disambiguationData":[TD([makeQuery(id+"F11.opExtrude","SWEPT_FACE",FACE,{"disambiguationData":[OSD([subQ4])]})])],"derivedFrom":makeQuery(id+"F9.boolean.opBoolean","SPLIT",EDGE,{"disambiguationData":[TD([makeQuery(id+"F9.opExtrude","SWEPT_FACE",FACE,{"disambiguationData":[OSD([subQ7])]})])],"derivedFrom":makeQuery(id+"F5.opExtrude","SWEPT_EDGE",EDGE,{"disambiguationData":[OSD([subQ1,subQ0])]})})});}
            var Q1;
            {var subQ0=sQuery(id+"F4.wireOp",EDGE,"E2.left");var subQ3=sQuery(id+"F4.wireOp",EDGE,"E2.bottom");var subQ6=sQuery(id+"F8.wireOp",EDGE,"E6");var subQ9=sQuery(id+"F10.wireOp",EDGE,"E18");Q1=makeQuery(id+"F11.boolean.opBoolean","SPLIT",EDGE,{"disambiguationData":[TD([makeQuery(id+"F11.opExtrude","SWEPT_FACE",FACE,{"disambiguationData":[OSD([subQ9])]})])],"derivedFrom":makeQuery(id+"F9.boolean.opBoolean","SPLIT",EDGE,{"disambiguationData":[TD([makeQuery(id+"F9.opExtrude","SWEPT_FACE",FACE,{"disambiguationData":[OSD([subQ6])]})])],"derivedFrom":makeQuery(id+"F5.opExtrude","SWEPT_EDGE",EDGE,{"disambiguationData":[OSD([subQ3,subQ0])]})})});}
            var Q2;
            {var subQ0=sQuery(id+"F4.wireOp",EDGE,"E2.right");var subQ2=sQuery(id+"F15.wireOp",EDGE,"E35");var subQ3=sQuery(id+"F4.wireOp",EDGE,"E2.top");Q2=makeQuery(id+"F16.boolean.opBoolean","SPLIT",EDGE,{"disambiguationData":[TD([makeQuery(id+"F16.opExtrude","SWEPT_FACE",FACE,{"disambiguationData":[OSD([subQ2])]})])],"derivedFrom":makeQuery(id+"F5.opExtrude","SWEPT_EDGE",EDGE,{"disambiguationData":[OSD([subQ3,subQ0])]})});}
            var Q3;
            {var subQ0=sQuery(id+"F4.wireOp",EDGE,"E2.left");var subQ1=sQuery(id+"F4.wireOp",EDGE,"E2.top");var subQ4=sQuery(id+"F15.wireOp",EDGE,"E35");Q3=makeQuery(id+"F16.boolean.opBoolean","SPLIT",EDGE,{"disambiguationData":[TD([makeQuery(id+"F16.opExtrude","SWEPT_FACE",FACE,{"disambiguationData":[OSD([subQ4])]})])],"derivedFrom":makeQuery(id+"F5.opExtrude","SWEPT_EDGE",EDGE,{"disambiguationData":[OSD([subQ1,subQ0])]})});}
            fillet(context, id + "F43", {"entities" : qUnion([Q0, Q1, Q2, Q3]), "radius" : 7 * mm, "tangentPropagation" : true, "allowEdgeOverflow" : false});
        }
        {
            var Q0;
            {var subQ0=sQuery(id+"F4.wireOp",EDGE,"E2.left");var subQ1=sQuery(id+"F4.wireOp",EDGE,"E2.top");var subQ2=sQuery(id+"F4.wireOp",EDGE,"E2.bottom");Q0=makeQuery(id+"F40.boolean.opBoolean","MERGE",FACE,{"derivedFrom":[makeQuery(id+"F34.boolean.opBoolean","MERGE",FACE,{"derivedFrom":[makeQuery(id+"F16.boolean.opBoolean","MERGE",FACE,{"derivedFrom":[makeQuery(id+"F14.boolean.opBoolean","MERGE",FACE,{"derivedFrom":[makeQuery(id+"F11.boolean.opBoolean","MERGE",FACE,{"derivedFrom":[makeQuery(id+"F9.boolean.opBoolean","MERGE",FACE,{"derivedFrom":[makeQuery(id+"F7.boolean.opBoolean","MERGE",FACE,{"derivedFrom":[makeQuery(id+"F5.opExtrude","SWEPT_FACE",FACE,{"disambiguationData":[OSD([subQ0])]}),makeQuery(id+"F7.opExtrude","CAP_FACE",FACE,{"disambiguationData":[OSD([subQ2,sQuery(id+"F4.wireOp",EDGE,"E2.right"),sQuery(id+"F6.wireOp",EDGE,"E3"),sQuery(id+"F6.wireOp",EDGE,"E4"),sQuery(id+"F6.wireOp",EDGE,"E5")])],"isStart":false})]}),makeQuery(id+"F9.opExtrude","CAP_FACE",FACE,{"disambiguationData":[OSD([sQuery(id+"F8.wireOp",EDGE,"E6"),sQuery(id+"F8.wireOp",EDGE,"E7"),sQuery(id+"F8.wireOp",EDGE,"E8"),sQuery(id+"F8.wireOp",EDGE,"E9")])],"isStart":false})]}),makeQuery(id+"F11.opExtrude","CAP_FACE",FACE,{"disambiguationData":[OSD([sQuery(id+"F10.wireOp",EDGE,"E11"),sQuery(id+"F10.wireOp",EDGE,"E12"),sQuery(id+"F10.wireOp",EDGE,"E13"),sQuery(id+"F10.wireOp",EDGE,"E14"),sQuery(id+"F10.wireOp",EDGE,"E15"),sQuery(id+"F10.wireOp",EDGE,"E16"),sQuery(id+"F10.wireOp",EDGE,"E17"),sQuery(id+"F10.wireOp",EDGE,"E18"),sQuery(id+"F10.wireOp",EDGE,"E19")])],"isStart":true})]}),makeQuery(id+"F14.opExtrude","CAP_FACE",FACE,{"disambiguationData":[OSD([subQ2,subQ0,sQuery(id+"F13.wireOp",EDGE,"E26"),sQuery(id+"F13.wireOp",EDGE,"E27"),sQuery(id+"F13.wireOp",EDGE,"E28")])],"isStart":true})]}),makeQuery(id+"F16.opExtrude","CAP_FACE",FACE,{"disambiguationData":[OSD([subQ1,subQ0,sQuery(id+"F15.wireOp",EDGE,"E29"),sQuery(id+"F15.wireOp",EDGE,"E30"),sQuery(id+"F15.wireOp",EDGE,"E31")])],"isStart":true}),makeQuery(id+"F16.opExtrude","CAP_FACE",FACE,{"disambiguationData":[OSD([subQ1,subQ0,sQuery(id+"F15.wireOp",EDGE,"E33"),sQuery(id+"F15.wireOp",EDGE,"E34"),sQuery(id+"F15.wireOp",EDGE,"E35")])],"isStart":true})]}),makeQuery(id+"F34.opExtrude","CAP_FACE",FACE,{"disambiguationData":[OSD([sQuery(id+"F33.wireOp",EDGE,"E55"),sQuery(id+"F33.wireOp",EDGE,"E58"),sQuery(id+"F33.wireOp",EDGE,"E59"),sQuery(id+"F33.wireOp",EDGE,"E60"),sQuery(id+"F33.wireOp",EDGE,"E61")])],"isStart":true})]}),makeQuery(id+"F40.opExtrude","CAP_FACE",FACE,{"disambiguationData":[OSD([sQuery(id+"F38.wireOp",EDGE,"E70"),sQuery(id+"F38.wireOp",EDGE,"E71"),sQuery(id+"F38.wireOp",EDGE,"E72")])],"isStart":false})]});}
            var sketch = newSketch(context, id + "F44", { "sketchPlane" : qUnion([Q0])});
            skCircle(sketch, "E74", {"center": v(-247.4, -0.32) * mm, "radius": 2.16 * mm});
            skSolve(sketch);
        }
        {
            var Q0;
            Q0 = qSketchRegion(id + "F44", true);
            extrude(context, id + "F45", {"entities" : qUnion([Q0]), "operationType" : NewBodyOperationType.ADD, "depth" : 6.35 * mm});
        }
        {
            var Q0;
            Q0=makeQuery(id+"F5.opExtrude","CAP_FACE",FACE,{"disambiguationData":[OSD([sQuery(id+"F4.wireOp",EDGE,"E2.bottom"),sQuery(id+"F4.wireOp",EDGE,"E2.top"),sQuery(id+"F4.wireOp",EDGE,"E2.left"),sQuery(id+"F4.wireOp",EDGE,"E2.right")])],"isStart":true});
            var sketch = newSketch(context, id + "F46", { "sketchPlane" : qUnion([Q0])});
            skCircle(sketch, "E75", {"center": v(0, 0) * mm, "radius": 3.18 * mm});
            skCircle(sketch, "E76", {"center": v(0, 0) * mm, "radius": 5.72 * mm});
            skSolve(sketch);
        }
        {
            var Q0;
            Q0 = qSketchRegion(id + "F46", true);
            extrude(context, id + "F47", {"entities" : qUnion([Q0]), "operationType" : NewBodyOperationType.REMOVE, "oppositeDirection" : true, "depth" : 50.8 * mm});
        }
        {
            var Q0;
            {var subQ0=sQuery(id+"F4.wireOp",EDGE,"E2.left");var subQ1=sQuery(id+"F4.wireOp",EDGE,"E2.top");var subQ2=sQuery(id+"F4.wireOp",EDGE,"E2.bottom");Q0=makeQuery(id+"F40.boolean.opBoolean","MERGE",FACE,{"derivedFrom":[makeQuery(id+"F34.boolean.opBoolean","MERGE",FACE,{"derivedFrom":[makeQuery(id+"F16.boolean.opBoolean","MERGE",FACE,{"derivedFrom":[makeQuery(id+"F14.boolean.opBoolean","MERGE",FACE,{"derivedFrom":[makeQuery(id+"F11.boolean.opBoolean","MERGE",FACE,{"derivedFrom":[makeQuery(id+"F9.boolean.opBoolean","MERGE",FACE,{"derivedFrom":[makeQuery(id+"F7.boolean.opBoolean","MERGE",FACE,{"derivedFrom":[makeQuery(id+"F5.opExtrude","SWEPT_FACE",FACE,{"disambiguationData":[OSD([subQ0])]}),makeQuery(id+"F7.opExtrude","CAP_FACE",FACE,{"disambiguationData":[OSD([subQ2,sQuery(id+"F4.wireOp",EDGE,"E2.right"),sQuery(id+"F6.wireOp",EDGE,"E3"),sQuery(id+"F6.wireOp",EDGE,"E4"),sQuery(id+"F6.wireOp",EDGE,"E5")])],"isStart":false})]}),makeQuery(id+"F9.opExtrude","CAP_FACE",FACE,{"disambiguationData":[OSD([sQuery(id+"F8.wireOp",EDGE,"E6"),sQuery(id+"F8.wireOp",EDGE,"E7"),sQuery(id+"F8.wireOp",EDGE,"E8"),sQuery(id+"F8.wireOp",EDGE,"E9")])],"isStart":false})]}),makeQuery(id+"F11.opExtrude","CAP_FACE",FACE,{"disambiguationData":[OSD([sQuery(id+"F10.wireOp",EDGE,"E11"),sQuery(id+"F10.wireOp",EDGE,"E12"),sQuery(id+"F10.wireOp",EDGE,"E13"),sQuery(id+"F10.wireOp",EDGE,"E14"),sQuery(id+"F10.wireOp",EDGE,"E15"),sQuery(id+"F10.wireOp",EDGE,"E16"),sQuery(id+"F10.wireOp",EDGE,"E17"),sQuery(id+"F10.wireOp",EDGE,"E18"),sQuery(id+"F10.wireOp",EDGE,"E19")])],"isStart":true})]}),makeQuery(id+"F14.opExtrude","CAP_FACE",FACE,{"disambiguationData":[OSD([subQ2,subQ0,sQuery(id+"F13.wireOp",EDGE,"E26"),sQuery(id+"F13.wireOp",EDGE,"E27"),sQuery(id+"F13.wireOp",EDGE,"E28")])],"isStart":true})]}),makeQuery(id+"F16.opExtrude","CAP_FACE",FACE,{"disambiguationData":[OSD([subQ1,subQ0,sQuery(id+"F15.wireOp",EDGE,"E29"),sQuery(id+"F15.wireOp",EDGE,"E30"),sQuery(id+"F15.wireOp",EDGE,"E31")])],"isStart":true}),makeQuery(id+"F16.opExtrude","CAP_FACE",FACE,{"disambiguationData":[OSD([subQ1,subQ0,sQuery(id+"F15.wireOp",EDGE,"E33"),sQuery(id+"F15.wireOp",EDGE,"E34"),sQuery(id+"F15.wireOp",EDGE,"E35")])],"isStart":true})]}),makeQuery(id+"F34.opExtrude","CAP_FACE",FACE,{"disambiguationData":[OSD([sQuery(id+"F33.wireOp",EDGE,"E55"),sQuery(id+"F33.wireOp",EDGE,"E58"),sQuery(id+"F33.wireOp",EDGE,"E59"),sQuery(id+"F33.wireOp",EDGE,"E60"),sQuery(id+"F33.wireOp",EDGE,"E61")])],"isStart":true})]}),makeQuery(id+"F40.opExtrude","CAP_FACE",FACE,{"disambiguationData":[OSD([sQuery(id+"F38.wireOp",EDGE,"E70"),sQuery(id+"F38.wireOp",EDGE,"E71"),sQuery(id+"F38.wireOp",EDGE,"E72")])],"isStart":false})]});}
            var sketch = newSketch(context, id + "F48", { "sketchPlane" : qUnion([Q0])});
            skLineSegment(sketch, "E77", {"start": v(-234.95, 0) * mm, "end": v(-190.5, 0) * mm});
            skLineSegment(sketch, "E78", {"start": v(-234.95, 0) * mm, "end": v(-212.72, 0) * mm});
            skLineSegment(sketch, "E79", {"start": v(-212.72, 0) * mm, "end": v(-190.5, 0) * mm});
            skLineSegment(sketch, "E80", {"start": v(-190.5, 0) * mm, "end": v(-201.61, 0) * mm});
            skLineSegment(sketch, "E81", {"start": v(-201.61, 0) * mm, "end": v(-212.72, 0) * mm});
            skLineSegment(sketch, "E82", {"start": v(-212.72, 0) * mm, "end": v(-223.84, 0) * mm});
            skLineSegment(sketch, "E83", {"start": v(-223.84, 0) * mm, "end": v(-234.95, 0) * mm});
            skLineSegment(sketch, "E84", {"start": v(-234.95, 0) * mm, "end": v(-229.4, 0) * mm});
            skLineSegment(sketch, "E85", {"start": v(-229.4, 0) * mm, "end": v(-223.84, 0) * mm});
            skLineSegment(sketch, "E86", {"start": v(-223.84, 0) * mm, "end": v(-218.28, 0) * mm});
            skLineSegment(sketch, "E87", {"start": v(-218.28, 0) * mm, "end": v(-212.72, 0) * mm});
            skLineSegment(sketch, "E88", {"start": v(-212.72, 0) * mm, "end": v(-207.17, 0) * mm});
            skLineSegment(sketch, "E89", {"start": v(-207.17, 0) * mm, "end": v(-201.61, 0) * mm});
            skLineSegment(sketch, "E90", {"start": v(-201.61, 0) * mm, "end": v(-196.06, 0) * mm});
            skCircle(sketch, "E91", {"center": v(-229.4, 0) * mm, "radius": 1.27 * mm});
            skCircle(sketch, "E92", {"center": v(-223.84, 0) * mm, "radius": 1.27 * mm});
            skCircle(sketch, "E93", {"center": v(-218.28, 0) * mm, "radius": 1.27 * mm});
            skCircle(sketch, "E94", {"center": v(-212.72, 0) * mm, "radius": 1.27 * mm});
            skCircle(sketch, "E95", {"center": v(-207.17, 0) * mm, "radius": 1.27 * mm});
            skCircle(sketch, "E96", {"center": v(-201.61, 0) * mm, "radius": 1.27 * mm});
            skCircle(sketch, "E97", {"center": v(-196.06, 0) * mm, "radius": 1.27 * mm});
            skSolve(sketch);
        }
        {
            var Q0;
            Q0 = qSketchRegion(id + "F48", true);
            extrude(context, id + "F49", {"entities" : qUnion([Q0]), "operationType" : NewBodyOperationType.REMOVE, "oppositeDirection" : true, "depth" : 2.54 * mm});
        }
        {
            var Q0;
            {var subQ0=sQuery(id+"F4.wireOp",EDGE,"E2.left");var subQ1=sQuery(id+"F4.wireOp",EDGE,"E2.top");var subQ2=sQuery(id+"F4.wireOp",EDGE,"E2.bottom");var subQ3=sQuery(id+"F4.wireOp",EDGE,"E2.right");Q0=makeQuery(id+"F39.boolean.opBoolean","MERGE",FACE,{"derivedFrom":[makeQuery(id+"F34.boolean.opBoolean","MERGE",FACE,{"derivedFrom":[makeQuery(id+"F16.boolean.opBoolean","MERGE",FACE,{"derivedFrom":[makeQuery(id+"F14.boolean.opBoolean","MERGE",FACE,{"derivedFrom":[makeQuery(id+"F11.boolean.opBoolean","MERGE",FACE,{"derivedFrom":[makeQuery(id+"F9.boolean.opBoolean","MERGE",FACE,{"derivedFrom":[makeQuery(id+"F7.boolean.opBoolean","MERGE",FACE,{"derivedFrom":[makeQuery(id+"F5.opExtrude","SWEPT_FACE",FACE,{"disambiguationData":[OSD([subQ3])]}),makeQuery(id+"F7.opExtrude","CAP_FACE",FACE,{"disambiguationData":[OSD([subQ2,subQ3,sQuery(id+"F6.wireOp",EDGE,"E3"),sQuery(id+"F6.wireOp",EDGE,"E4"),sQuery(id+"F6.wireOp",EDGE,"E5")])],"isStart":true})]}),makeQuery(id+"F9.opExtrude","CAP_FACE",FACE,{"disambiguationData":[OSD([sQuery(id+"F8.wireOp",EDGE,"E6"),sQuery(id+"F8.wireOp",EDGE,"E7"),sQuery(id+"F8.wireOp",EDGE,"E8"),sQuery(id+"F8.wireOp",EDGE,"E9")])],"isStart":true})]}),makeQuery(id+"F11.opExtrude","CAP_FACE",FACE,{"disambiguationData":[OSD([sQuery(id+"F10.wireOp",EDGE,"E11"),sQuery(id+"F10.wireOp",EDGE,"E12"),sQuery(id+"F10.wireOp",EDGE,"E13"),sQuery(id+"F10.wireOp",EDGE,"E14"),sQuery(id+"F10.wireOp",EDGE,"E15"),sQuery(id+"F10.wireOp",EDGE,"E16"),sQuery(id+"F10.wireOp",EDGE,"E17"),sQuery(id+"F10.wireOp",EDGE,"E18"),sQuery(id+"F10.wireOp",EDGE,"E19")])],"isStart":false})]}),makeQuery(id+"F14.opExtrude","CAP_FACE",FACE,{"disambiguationData":[OSD([subQ2,subQ0,sQuery(id+"F13.wireOp",EDGE,"E26"),sQuery(id+"F13.wireOp",EDGE,"E27"),sQuery(id+"F13.wireOp",EDGE,"E28")])],"isStart":false})]}),makeQuery(id+"F16.opExtrude","CAP_FACE",FACE,{"disambiguationData":[OSD([subQ1,subQ0,sQuery(id+"F15.wireOp",EDGE,"E29"),sQuery(id+"F15.wireOp",EDGE,"E30"),sQuery(id+"F15.wireOp",EDGE,"E31")])],"isStart":false}),makeQuery(id+"F16.opExtrude","CAP_FACE",FACE,{"disambiguationData":[OSD([subQ1,subQ0,sQuery(id+"F15.wireOp",EDGE,"E33"),sQuery(id+"F15.wireOp",EDGE,"E34"),sQuery(id+"F15.wireOp",EDGE,"E35")])],"isStart":false})]}),makeQuery(id+"F34.opExtrude","CAP_FACE",FACE,{"disambiguationData":[OSD([sQuery(id+"F33.wireOp",EDGE,"E55"),sQuery(id+"F33.wireOp",EDGE,"E58"),sQuery(id+"F33.wireOp",EDGE,"E59"),sQuery(id+"F33.wireOp",EDGE,"E60"),sQuery(id+"F33.wireOp",EDGE,"E61")])],"isStart":false})]}),makeQuery(id+"F39.opExtrude","CAP_FACE",FACE,{"disambiguationData":[OSD([sQuery(id+"F38.wireOp",EDGE,"E70"),sQuery(id+"F38.wireOp",EDGE,"E71"),sQuery(id+"F38.wireOp",EDGE,"E72")])],"isStart":false})]});}
            var sketch = newSketch(context, id + "F50", { "sketchPlane" : qUnion([Q0])});
            skLineSegment(sketch, "E98", {"start": v(234.95, 0) * mm, "end": v(190.5, 0) * mm});
            skLineSegment(sketch, "E99", {"start": v(234.95, 0) * mm, "end": v(212.72, 0) * mm});
            skLineSegment(sketch, "E100", {"start": v(212.72, 0) * mm, "end": v(223.84, 0) * mm});
            skLineSegment(sketch, "E101", {"start": v(223.84, 0) * mm, "end": v(212.72, 0) * mm});
            skLineSegment(sketch, "E102", {"start": v(212.72, 0) * mm, "end": v(190.5, 0) * mm});
            skLineSegment(sketch, "E103", {"start": v(190.5, 0) * mm, "end": v(201.61, 0) * mm});
            skLineSegment(sketch, "E104", {"start": v(201.61, 0) * mm, "end": v(212.72, 0) * mm});
            skLineSegment(sketch, "E105", {"start": v(234.95, 0) * mm, "end": v(223.84, 0) * mm});
            skLineSegment(sketch, "E106", {"start": v(234.95, 0) * mm, "end": v(229.4, 0) * mm});
            skLineSegment(sketch, "E107", {"start": v(229.4, 0) * mm, "end": v(223.84, 0) * mm});
            skLineSegment(sketch, "E108", {"start": v(223.84, 0) * mm, "end": v(218.28, 0) * mm});
            skLineSegment(sketch, "E109", {"start": v(218.28, 0) * mm, "end": v(212.72, 0) * mm});
            skLineSegment(sketch, "E110", {"start": v(212.72, 0) * mm, "end": v(207.17, 0) * mm});
            skLineSegment(sketch, "E111", {"start": v(207.17, 0) * mm, "end": v(201.61, 0) * mm});
            skLineSegment(sketch, "E112", {"start": v(201.61, 0) * mm, "end": v(196.06, 0) * mm});
            skCircle(sketch, "E113", {"center": v(229.4, 0) * mm, "radius": 1.27 * mm});
            skCircle(sketch, "E114", {"center": v(223.84, 0) * mm, "radius": 1.27 * mm});
            skCircle(sketch, "E115", {"center": v(218.28, 0) * mm, "radius": 1.27 * mm});
            skCircle(sketch, "E116", {"center": v(212.72, 0) * mm, "radius": 1.27 * mm});
            skCircle(sketch, "E117", {"center": v(207.17, 0) * mm, "radius": 1.27 * mm});
            skCircle(sketch, "E118", {"center": v(201.61, 0) * mm, "radius": 1.27 * mm});
            skCircle(sketch, "E119", {"center": v(196.06, 0) * mm, "radius": 1.27 * mm});
            skSolve(sketch);
        }
        {
            var Q0;
            Q0 = qSketchRegion(id + "F50", true);
            extrude(context, id + "F51", {"entities" : qUnion([Q0]), "operationType" : NewBodyOperationType.REMOVE, "oppositeDirection" : true, "depth" : 2.54 * mm});
        }
        {
            var Q0;
            Q0=makeQuery(id+"F20.boolean.opBoolean","COPY",FACE,{"derivedFrom":makeQuery(id+"F20.opExtrude","CAP_FACE",FACE,{"disambiguationData":[OSD([sQuery(id+"F19.wireOp",EDGE,"E38"),sQuery(id+"F19.wireOp",EDGE,"E42"),sQuery(id+"F19.wireOp",EDGE,"E43"),sQuery(id+"F19.wireOp",EDGE,"E44")])],"isStart":false})});
            var sketch = newSketch(context, id + "F52", { "sketchPlane" : qUnion([Q0])});
            skLineSegment(sketch, "E120", {"start": v(-3.5, -283.21) * mm, "end": v(-3.5, -250.2) * mm});
            skLineSegment(sketch, "E121", {"start": v(3.5, -283.21) * mm, "end": v(3.5, -250.2) * mm});
            skLineSegment(sketch, "E122", {"start": v(-3.5, -283.21) * mm, "end": v(3.5, -283.21) * mm});
            skLineSegment(sketch, "E123", {"start": v(-3.5, -250.2) * mm, "end": v(3.5, -250.2) * mm});
            skSolve(sketch);
        }
        {
            var Q0;
            Q0 = qSketchRegion(id + "F52", true);
            extrude(context, id + "F53", {"entities" : qUnion([Q0]), "operationType" : NewBodyOperationType.REMOVE, "oppositeDirection" : true, "depth" : 10.16 * mm});
        }
        {
            var Q0;
            Q0=makeQuery(id+"F1.opExtrude","SWEPT_EDGE",EDGE,{"disambiguationData":[OSD([sQuery(id+"F0.wireOp",EDGE,"E0.top"),sQuery(id+"F0.wireOp",EDGE,"E0.right")])]});
            var Q1;
            Q1=makeQuery(id+"F1.opExtrude","SWEPT_EDGE",EDGE,{"disambiguationData":[OSD([sQuery(id+"F0.wireOp",EDGE,"E0.bottom"),sQuery(id+"F0.wireOp",EDGE,"E0.right")])]});
            var Q2;
            Q2=makeQuery(id+"F1.opExtrude","SWEPT_EDGE",EDGE,{"disambiguationData":[OSD([sQuery(id+"F0.wireOp",EDGE,"E0.bottom"),sQuery(id+"F0.wireOp",EDGE,"E0.left")])]});
            var Q3;
            Q3=makeQuery(id+"F1.opExtrude","SWEPT_EDGE",EDGE,{"disambiguationData":[OSD([sQuery(id+"F0.wireOp",EDGE,"E0.top"),sQuery(id+"F0.wireOp",EDGE,"E0.left")])]});
            chamfer(context, id + "F54", {"entities" : qUnion([Q0, Q1, Q2, Q3]), "width" : 1.27 * mm, "tangentPropagation" : true});
        }
        {
            var Q0;
            Q0=makeQuery(id+"F9.opExtrude","CAP_EDGE",EDGE,{"disambiguationData":[OSD([sQuery(id+"F8.wireOp",EDGE,"E8")])],"isStart":false});
            var Q1;
            Q1=makeQuery(id+"F9.opExtrude","CAP_EDGE",EDGE,{"disambiguationData":[OSD([sQuery(id+"F8.wireOp",EDGE,"E8")])],"isStart":true});
            var Q2;
            Q2=makeQuery(id+"F7.opExtrude","CAP_EDGE",EDGE,{"disambiguationData":[OSD([sQuery(id+"F6.wireOp",EDGE,"E5")])],"isStart":false});
            var Q3;
            Q3=makeQuery(id+"F7.opExtrude","CAP_EDGE",EDGE,{"disambiguationData":[OSD([sQuery(id+"F6.wireOp",EDGE,"E5")])],"isStart":true});
            var Q4;
            {var subQ0=sQuery(id+"F6.wireOp",EDGE,"E5");var subQ1=sQuery(id+"F4.wireOp",EDGE,"E2.right");var subQ2=sQuery(id+"F4.wireOp",EDGE,"E2.bottom");Q4=makeQuery(id+"F9.boolean.opBoolean","SPLIT",EDGE,{"disambiguationData":[TD([makeQuery(id+"F7.opExtrude","SWEPT_FACE",FACE,{"disambiguationData":[OSD([subQ0])]})])],"derivedFrom":makeQuery(id+"F5.opExtrude","SWEPT_EDGE",EDGE,{"disambiguationData":[OSD([subQ2,subQ1])]})});}
            var Q5;
            {var subQ0=sQuery(id+"F6.wireOp",EDGE,"E5");var subQ1=sQuery(id+"F4.wireOp",EDGE,"E2.bottom");var subQ2=sQuery(id+"F4.wireOp",EDGE,"E2.left");Q5=makeQuery(id+"F9.boolean.opBoolean","SPLIT",EDGE,{"disambiguationData":[TD([makeQuery(id+"F7.opExtrude","SWEPT_FACE",FACE,{"disambiguationData":[OSD([subQ0])]})])],"derivedFrom":makeQuery(id+"F5.opExtrude","SWEPT_EDGE",EDGE,{"disambiguationData":[OSD([subQ1,subQ2])]})});}
            chamfer(context, id + "F55", {"entities" : qUnion([Q0, Q1, Q2, Q3, Q4, Q5]), "width" : 2.54 * mm, "tangentPropagation" : true});
        }
    });
